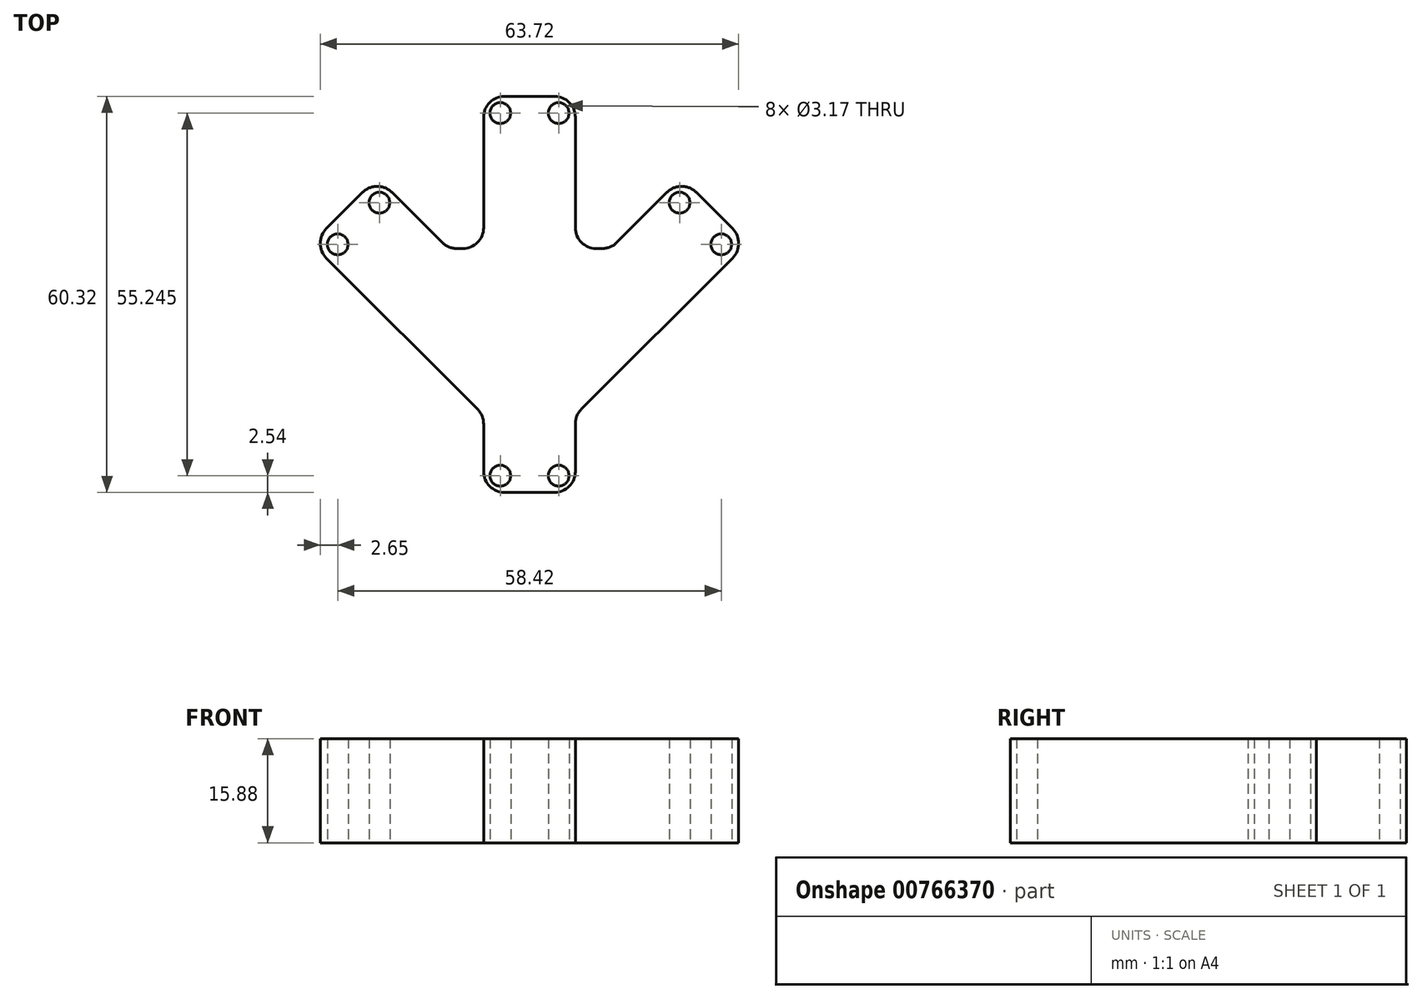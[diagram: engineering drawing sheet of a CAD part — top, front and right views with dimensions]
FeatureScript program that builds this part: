
annotation { "Feature Type Name" : "Feature", "Feature Type Description" : "" }
export const myFeature = defineFeature(function(context is Context, id is Id, definition is map)
    precondition{}
    {
        {
            var Q0;
            Q0=qCreatedBy(makeId("Top.planeOp"),FACE);
            var sketch = newSketch(context, id + "F0", { "sketchPlane" : qUnion([Q0])});
            skLineSegment(sketch, "E0", {"start": v(0.27, 0.13) * mm, "end": v(0.27, 0.41) * mm});
            skLineSegment(sketch, "E1", {"start": v(0.31, 0.5) * mm, "end": v(1.22, 1.4) * mm});
            skLineSegment(sketch, "E2", {"start": v(1.22, 1.58) * mm, "end": v(1, 1.8) * mm});
            skLineSegment(sketch, "E3", {"start": v(0.82, 1.8) * mm, "end": v(0.52, 1.5) * mm});
            skLineSegment(sketch, "E4", {"start": v(0.44, 1.46) * mm, "end": v(0.4, 1.46) * mm});
            skLineSegment(sketch, "E5", {"start": v(0.27, 1.59) * mm, "end": v(0.27, 2.25) * mm});
            skLineSegment(sketch, "E6", {"start": v(0.15, 2.38) * mm, "end": v(-0.15, 2.38) * mm});
            skLineSegment(sketch, "E7", {"start": v(-0.28, 2.25) * mm, "end": v(-0.28, 1.59) * mm});
            skLineSegment(sketch, "E8", {"start": v(-0.4, 1.46) * mm, "end": v(-0.44, 1.46) * mm});
            skLineSegment(sketch, "E9", {"start": v(-0.52, 1.5) * mm, "end": v(-0.82, 1.8) * mm});
            skLineSegment(sketch, "E10", {"start": v(-1, 1.8) * mm, "end": v(-1.22, 1.58) * mm});
            skLineSegment(sketch, "E11", {"start": v(-1.22, 1.4) * mm, "end": v(-0.31, 0.5) * mm});
            skLineSegment(sketch, "E12", {"start": v(-0.27, 0.41) * mm, "end": v(-0.27, 0.12) * mm});
            skLineSegment(sketch, "E13", {"start": v(-0.15, 0) * mm, "end": v(0.15, 0) * mm});
            skPoint(sketch, "E14.visualSharp", {"position": v(-0.49, 1.46) * mm});
            skArc(sketch, "E14.filletArc", {"start": v(-0.52, 1.5) * mm, "mid": v(-0.48, 1.47) * mm, "end": v(-0.44, 1.46) * mm});
            skPoint(sketch, "E15.visualSharp", {"position": v(-0.28, 1.46) * mm});
            skArc(sketch, "E15.filletArc", {"start": v(-0.4, 1.46) * mm, "mid": v(-0.31, 1.5) * mm, "end": v(-0.27, 1.59) * mm});
            skPoint(sketch, "E16.visualSharp", {"position": v(0.27, 1.46) * mm});
            skArc(sketch, "E16.filletArc", {"start": v(0.27, 1.59) * mm, "mid": v(0.31, 1.5) * mm, "end": v(0.4, 1.46) * mm});
            skPoint(sketch, "E17.visualSharp", {"position": v(0.49, 1.46) * mm});
            skArc(sketch, "E17.filletArc", {"start": v(0.44, 1.46) * mm, "mid": v(0.48, 1.47) * mm, "end": v(0.52, 1.5) * mm});
            skPoint(sketch, "E18.visualSharp", {"position": v(-0.28, 2.38) * mm});
            skArc(sketch, "E18.filletArc", {"start": v(-0.15, 2.37) * mm, "mid": v(-0.24, 2.34) * mm, "end": v(-0.27, 2.25) * mm});
            skPoint(sketch, "E19.visualSharp", {"position": v(0.27, 2.38) * mm});
            skArc(sketch, "E19.filletArc", {"start": v(0.27, 2.25) * mm, "mid": v(0.24, 2.34) * mm, "end": v(0.15, 2.38) * mm});
            skPoint(sketch, "E20.visualSharp", {"position": v(0.91, 1.89) * mm});
            skArc(sketch, "E20.filletArc", {"start": v(1, 1.8) * mm, "mid": v(0.91, 1.84) * mm, "end": v(0.82, 1.8) * mm});
            skPoint(sketch, "E21.visualSharp", {"position": v(1.3, 1.5) * mm});
            skArc(sketch, "E21.filletArc", {"start": v(1.22, 1.4) * mm, "mid": v(1.25, 1.5) * mm, "end": v(1.22, 1.58) * mm});
            skPoint(sketch, "E22.visualSharp", {"position": v(0.27, 0) * mm});
            skArc(sketch, "E22.filletArc", {"start": v(0.15, 0) * mm, "mid": v(0.24, 0.04) * mm, "end": v(0.27, 0.13) * mm});
            skPoint(sketch, "E23.visualSharp", {"position": v(-0.27, 0) * mm});
            skArc(sketch, "E23.filletArc", {"start": v(-0.27, 0.12) * mm, "mid": v(-0.24, 0.04) * mm, "end": v(-0.15, 0) * mm});
            skPoint(sketch, "E24.visualSharp", {"position": v(-0.28, 0.46) * mm});
            skArc(sketch, "E24.filletArc", {"start": v(-0.27, 0.41) * mm, "mid": v(-0.28, 0.46) * mm, "end": v(-0.31, 0.5) * mm});
            skPoint(sketch, "E25.visualSharp", {"position": v(-1.3, 1.5) * mm});
            skArc(sketch, "E25.filletArc", {"start": v(-1.22, 1.58) * mm, "mid": v(-1.25, 1.5) * mm, "end": v(-1.22, 1.4) * mm});
            skPoint(sketch, "E26.visualSharp", {"position": v(-0.91, 1.89) * mm});
            skArc(sketch, "E26.filletArc", {"start": v(-0.82, 1.8) * mm, "mid": v(-0.91, 1.84) * mm, "end": v(-1, 1.8) * mm});
            skPoint(sketch, "E27.visualSharp", {"position": v(0.28, 0.46) * mm});
            skArc(sketch, "E27.filletArc", {"start": v(0.31, 0.5) * mm, "mid": v(0.28, 0.46) * mm, "end": v(0.27, 0.41) * mm});
            skCircle(sketch, "E28", {"center": v(-0.17, 0.1) * mm, "radius": 0.06 * mm});
            skCircle(sketch, "E29.MirrorC", {"center": v(0.17, 0.1) * mm, "radius": 0.06 * mm});
            skCircle(sketch, "E30", {"center": v(-0.17, 2.27) * mm, "radius": 0.06 * mm});
            skCircle(sketch, "E31.MirrorC", {"center": v(0.17, 2.27) * mm, "radius": 0.06 * mm});
            skCircle(sketch, "E32", {"center": v(-0.9, 1.74) * mm, "radius": 0.06 * mm});
            skCircle(sketch, "E33.MirrorC", {"center": v(0.9, 1.74) * mm, "radius": 0.06 * mm});
            skCircle(sketch, "E34", {"center": v(-1.15, 1.49) * mm, "radius": 0.06 * mm});
            skCircle(sketch, "E35.MirrorC", {"center": v(1.15, 1.49) * mm, "radius": 0.06 * mm});
            skSolve(sketch);
        }
        {
            var Q0;
            Q0=makeQuery(id+"F0.imprint","IMPRINT",FACE,{"disambiguationData":[TD([[makeQuery(id+"F0.imprint","IMPRINT",EDGE,{"derivedFrom":sQuery(id+"F0.wireOp",EDGE,"E0")}),1.0]])]});
            extrude(context, id + "F1", {"entities" : qUnion([Q0]), "depth" : .625 * mm, "offsetDistance" : 25 * mm});
        }
        {
            var Q0;
            Q0=makeQuery(id+"F1.opExtrude","SWEPT_BODY",BODY,{"disambiguationData":[OSD([sQuery(id+"F0.wireOp",EDGE,"E0"),sQuery(id+"F0.wireOp",EDGE,"E1"),sQuery(id+"F0.wireOp",EDGE,"E2"),sQuery(id+"F0.wireOp",EDGE,"E3"),sQuery(id+"F0.wireOp",EDGE,"E4"),sQuery(id+"F0.wireOp",EDGE,"E5"),sQuery(id+"F0.wireOp",EDGE,"E6"),sQuery(id+"F0.wireOp",EDGE,"E7"),sQuery(id+"F0.wireOp",EDGE,"E8"),sQuery(id+"F0.wireOp",EDGE,"E9"),sQuery(id+"F0.wireOp",EDGE,"E10"),sQuery(id+"F0.wireOp",EDGE,"E11"),sQuery(id+"F0.wireOp",EDGE,"E12"),sQuery(id+"F0.wireOp",EDGE,"E13"),sQuery(id+"F0.wireOp",EDGE,"E14.filletArc"),sQuery(id+"F0.wireOp",EDGE,"E15.filletArc"),sQuery(id+"F0.wireOp",EDGE,"E16.filletArc"),sQuery(id+"F0.wireOp",EDGE,"E17.filletArc"),sQuery(id+"F0.wireOp",EDGE,"E18.filletArc"),sQuery(id+"F0.wireOp",EDGE,"E19.filletArc"),sQuery(id+"F0.wireOp",EDGE,"E20.filletArc"),sQuery(id+"F0.wireOp",EDGE,"E21.filletArc"),sQuery(id+"F0.wireOp",EDGE,"E22.filletArc"),sQuery(id+"F0.wireOp",EDGE,"E23.filletArc"),sQuery(id+"F0.wireOp",EDGE,"E24.filletArc"),sQuery(id+"F0.wireOp",EDGE,"E25.filletArc"),sQuery(id+"F0.wireOp",EDGE,"E26.filletArc"),sQuery(id+"F0.wireOp",EDGE,"E27.filletArc"),sQuery(id+"F0.wireOp",EDGE,"E28"),sQuery(id+"F0.wireOp",EDGE,"E29.MirrorC"),sQuery(id+"F0.wireOp",EDGE,"E30"),sQuery(id+"F0.wireOp",EDGE,"E31.MirrorC"),sQuery(id+"F0.wireOp",EDGE,"E32"),sQuery(id+"F0.wireOp",EDGE,"E33.MirrorC"),sQuery(id+"F0.wireOp",EDGE,"E34"),sQuery(id+"F0.wireOp",EDGE,"E35.MirrorC")])]});
            var Q1;
            Q1=qCreatedBy(makeId("Origin.pointOp"),VERTEX);
            transform(context, id + "F2", {"entities" : qUnion([Q0]), "transformType" : TransformType.SCALE_UNIFORMLY, "scale" : 25.4, "scalePoint" : qUnion([Q1]), "makeCopy" : false});
        }
    });
